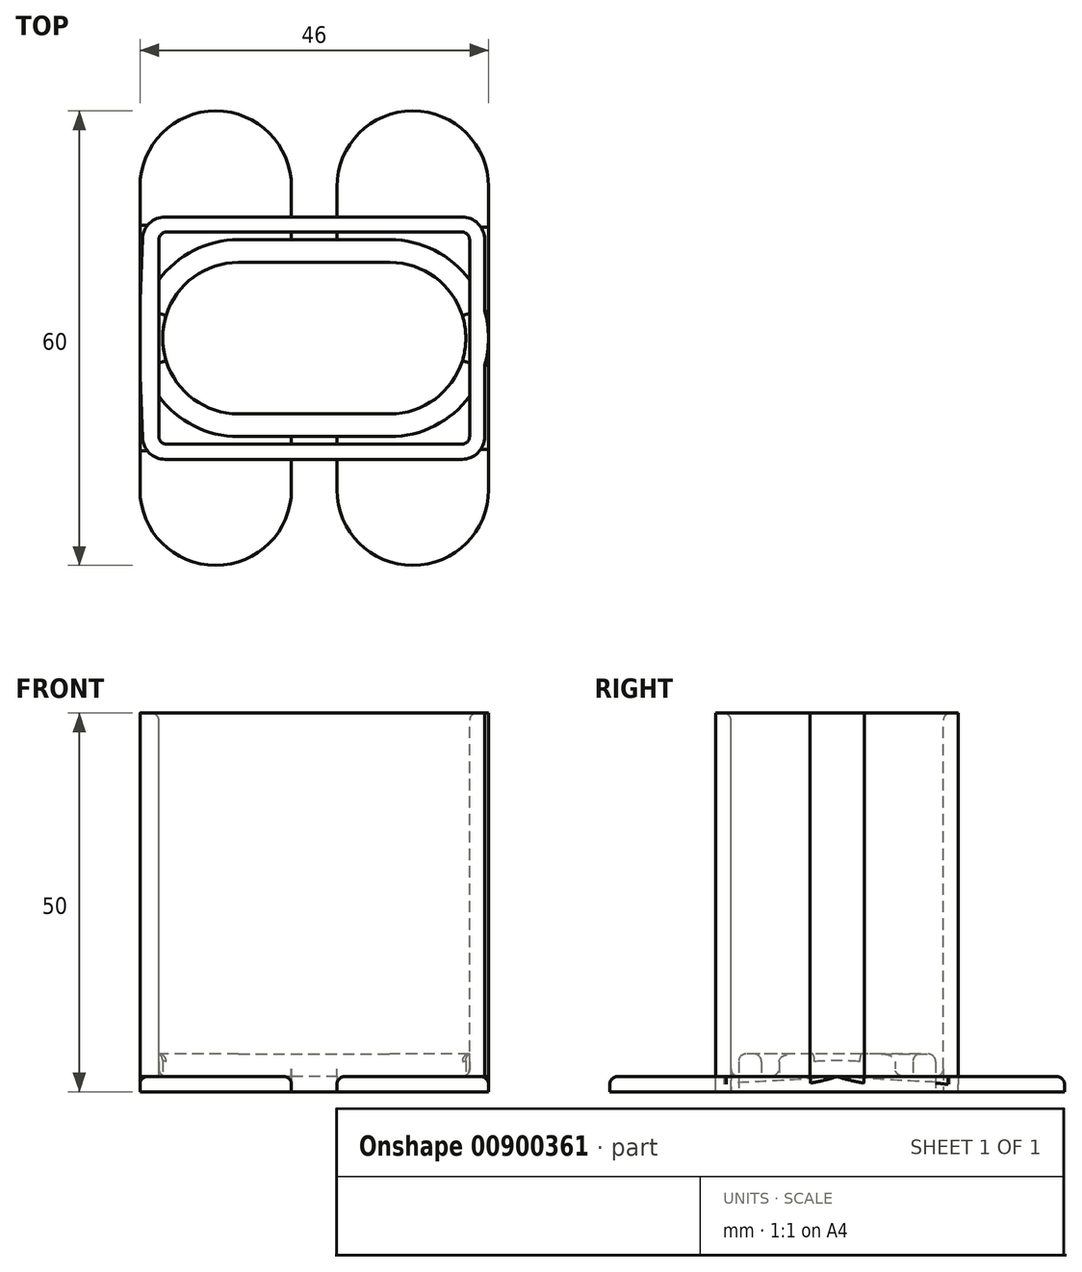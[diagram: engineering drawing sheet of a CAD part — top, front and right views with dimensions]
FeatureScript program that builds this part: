
annotation { "Feature Type Name" : "Feature", "Feature Type Description" : "" }
export const myFeature = defineFeature(function(context is Context, id is Id, definition is map)
    precondition{}
    {
        {
            var Q0;
            Q0=qCreatedBy(makeId("Top.planeOp"),FACE);
            var sketch = newSketch(context, id + "F0", { "sketchPlane" : qUnion([Q0])});
            skArc(sketch, "E0", {"start": v(-10, 10) * mm, "mid": v(-20, 0) * mm, "end": v(-10, -10) * mm});
            skLineSegment(sketch, "E1", {"start": v(-10, 10) * mm, "end": v(0, 10) * mm});
            skLineSegment(sketch, "E2", {"start": v(-10, -10) * mm, "end": v(0, -10) * mm});
            skArc(sketch, "E3", {"start": v(-10, 13) * mm, "mid": v(-23, 0) * mm, "end": v(-10, -13) * mm});
            skLineSegment(sketch, "E4", {"start": v(-10, 13) * mm, "end": v(0, 13) * mm});
            skLineSegment(sketch, "E5", {"start": v(-10, -13) * mm, "end": v(0, -13) * mm});
            skLineSegment(sketch, "E6", {"start": v(-23, 0) * mm, "end": v(-23, 20) * mm});
            skLineSegment(sketch, "E7", {"start": v(-23, 0) * mm, "end": v(-23, -20) * mm});
            skArc(sketch, "E8", {"start": v(-23, -20) * mm, "mid": v(-13, -30) * mm, "end": v(-3, -20) * mm});
            skArc(sketch, "E9", {"start": v(-3, 20) * mm, "mid": v(-13, 30) * mm, "end": v(-23, 20) * mm});
            skLineSegment(sketch, "E10", {"start": v(-3, 20) * mm, "end": v(-3, 13) * mm});
            skLineSegment(sketch, "E11", {"start": v(-3, -20) * mm, "end": v(-3, -13) * mm});
            skLineSegment(sketch, "E12.MirrorCS", {"start": v(3, -20) * mm, "end": v(3, -13) * mm});
            skLineSegment(sketch, "E13.MirrorCS", {"start": v(23, 0) * mm, "end": v(23, -20) * mm});
            skLineSegment(sketch, "E14.MirrorCS", {"start": v(10, -13) * mm, "end": v(0, -13) * mm});
            skArc(sketch, "E15.MirrorCS", {"start": v(23, -20) * mm, "mid": v(13, -30) * mm, "end": v(3, -20) * mm});
            skLineSegment(sketch, "E16.MirrorCS", {"start": v(3, 20) * mm, "end": v(3, 13) * mm});
            skLineSegment(sketch, "E17.MirrorCS", {"start": v(10, 10) * mm, "end": v(0, 10) * mm});
            skLineSegment(sketch, "E18.MirrorCS", {"start": v(10, 13) * mm, "end": v(0, 13) * mm});
            skArc(sketch, "E19.MirrorCS", {"start": v(10, 13) * mm, "mid": v(23, 0) * mm, "end": v(10, -13) * mm});
            skArc(sketch, "E20.MirrorCS", {"start": v(3, 20) * mm, "mid": v(13, 30) * mm, "end": v(23, 20) * mm});
            skArc(sketch, "E21.MirrorCS", {"start": v(10, 10) * mm, "mid": v(20, 0) * mm, "end": v(10, -10) * mm});
            skLineSegment(sketch, "E22.MirrorCS", {"start": v(23, 0) * mm, "end": v(23, 20) * mm});
            skLineSegment(sketch, "E23.MirrorCS", {"start": v(10, -10) * mm, "end": v(0, -10) * mm});
            skSolve(sketch);
        }
        {
            var Q0;
            Q0=makeQuery(id+"F0.imprint","IMPRINT",FACE,{"disambiguationData":[TD([[makeQuery(id+"F0.imprint","IMPRINT",EDGE,{"derivedFrom":sQuery(id+"F0.wireOp",EDGE,"E0")}),1.0]])]});
            var Q1;
            Q1=makeQuery(id+"F0.imprint","IMPRINT",FACE,{"disambiguationData":[TD([[makeQuery(id+"F0.imprint","IMPRINT",EDGE,{"derivedFrom":sQuery(id+"F0.wireOp",EDGE,"E0")}),-1.0]])]});
            var Q2;
            {var subQ0=sQuery(id+"F0.wireOp",EDGE,"E6");Q2=makeQuery(id+"F0.imprint","IMPRINT",FACE,{"disambiguationData":[TD([[makeQuery(id+"F0.imprint","IMPRINT",EDGE,{"derivedFrom":subQ0}),-1.0]])]});}
            var Q3;
            {var subQ0=sQuery(id+"F0.wireOp",EDGE,"E7");Q3=makeQuery(id+"F0.imprint","IMPRINT",FACE,{"disambiguationData":[TD([[makeQuery(id+"F0.imprint","IMPRINT",EDGE,{"derivedFrom":subQ0}),1.0]])]});}
            var Q4;
            {var subQ1=sQuery(id+"F0.wireOp",EDGE,"E12.MirrorCS");Q4=makeQuery(id+"F0.imprint","IMPRINT",FACE,{"disambiguationData":[TD([[makeQuery(id+"F0.imprint","IMPRINT",EDGE,{"derivedFrom":subQ1}),-1.0]])]});}
            var Q5;
            {var subQ4=sQuery(id+"F0.wireOp",EDGE,"E16.MirrorCS");Q5=makeQuery(id+"F0.imprint","IMPRINT",FACE,{"disambiguationData":[TD([[makeQuery(id+"F0.imprint","IMPRINT",EDGE,{"derivedFrom":subQ4}),1.0]])]});}
            extrude(context, id + "F1", {"entities" : qUnion([Q0, Q1, Q2, Q3, Q4, Q5]), "depth" : 2 * mm, "offsetDistance" : 25 * mm});
        }
        {
            var Q0;
            Q0=makeQuery(id+"F0.imprint","IMPRINT",FACE,{"disambiguationData":[TD([[makeQuery(id+"F0.imprint","IMPRINT",EDGE,{"derivedFrom":sQuery(id+"F0.wireOp",EDGE,"E0")}),-1.0]])]});
            extrude(context, id + "F2", {"entities" : qUnion([Q0]), "operationType" : NewBodyOperationType.ADD, "depth" : (2 + 3) * mm, "offsetDistance" : 25 * mm});
        }
        {
            var Q0;
            Q0=makeQuery(id+"F2.opExtrude","CAP_FACE",FACE,{"disambiguationData":[OSD([sQuery(id+"F0.wireOp",EDGE,"E0"),sQuery(id+"F0.wireOp",EDGE,"E1"),sQuery(id+"F0.wireOp",EDGE,"E2"),sQuery(id+"F0.wireOp",EDGE,"E3"),sQuery(id+"F0.wireOp",EDGE,"E4"),sQuery(id+"F0.wireOp",EDGE,"E5"),sQuery(id+"F0.wireOp",EDGE,"E14.MirrorCS"),sQuery(id+"F0.wireOp",EDGE,"E17.MirrorCS"),sQuery(id+"F0.wireOp",EDGE,"E18.MirrorCS"),sQuery(id+"F0.wireOp",EDGE,"E19.MirrorCS"),sQuery(id+"F0.wireOp",EDGE,"E21.MirrorCS"),sQuery(id+"F0.wireOp",EDGE,"E23.MirrorCS")])],"isStart":false});
            var sketch = newSketch(context, id + "F3", { "sketchPlane" : qUnion([Q0])});
            skLineSegment(sketch, "E24.bottom", {"start": v(-20.5, 14) * mm, "end": v(20.5, 14) * mm});
            skLineSegment(sketch, "E24.top", {"start": v(-20.5, -14) * mm, "end": v(20.5, -14) * mm});
            skLineSegment(sketch, "E24.left", {"start": v(-20.5, 14) * mm, "end": v(-20.5, -14) * mm});
            skLineSegment(sketch, "E24.right", {"start": v(20.5, 14) * mm, "end": v(20.5, -14) * mm});
            skPoint(sketch, "E25", {"position": v(0, 14) * mm});
            skPoint(sketch, "E26", {"position": v(20.5, 0) * mm});
            skLineSegment(sketch, "E27.bottom", {"start": v(-22.5, 16) * mm, "end": v(22.5, 16) * mm});
            skLineSegment(sketch, "E27.top", {"start": v(-22.5, -16) * mm, "end": v(22.5, -16) * mm});
            skLineSegment(sketch, "E27.left", {"start": v(-22.5, 16) * mm, "end": v(-22.5, -16) * mm});
            skLineSegment(sketch, "E27.right", {"start": v(22.5, 16) * mm, "end": v(22.5, -16) * mm});
            skPoint(sketch, "E27.middle", {"position": v(0, 0) * mm});
            skArc(sketch, "E28", {"start": v(-22.5, 16) * mm, "mid": v(-23, 0) * mm, "end": v(-22.5, -16) * mm});
            skArc(sketch, "E29", {"start": v(22.5, -16) * mm, "mid": v(23, 0) * mm, "end": v(22.5, 16) * mm});
            skSolve(sketch);
        }
        {
            var Q0;
            {var subQ0=sQuery(id+"F3.wireOp",EDGE,"E28");var subQ3=makeQuery(id+"F2.opExtrude","CAP_EDGE",EDGE,{"disambiguationData":[OSD([sQuery(id+"F0.wireOp",EDGE,"E3")])],"isStart":false});var subQ5=makeQuery(id+"F3.imprint","INTERSECT",VERTEX,{"derivedFrom":[subQ3,subQ0]});Q0=makeQuery(id+"F3.imprint","IMPRINT",FACE,{"disambiguationData":[TD([[makeQuery(id+"F3.imprint","IMPRINT",EDGE,{"disambiguationData":[TD([[subQ5,1.0]])],"derivedFrom":subQ3}),-1.0]])]});}
            var Q1;
            {var subQ0=sQuery(id+"F3.wireOp",EDGE,"E27.left");var subQ1=makeQuery(id+"F2.opExtrude","CAP_EDGE",EDGE,{"disambiguationData":[OSD([sQuery(id+"F0.wireOp",EDGE,"E3")])],"isStart":false});var subQ2=makeQuery(id+"F3.imprint","INTERSECT",VERTEX,{"disambiguationData":[OD(0.0)],"derivedFrom":[subQ1,subQ0]});Q1=makeQuery(id+"F3.imprint","IMPRINT",FACE,{"disambiguationData":[TD([[makeQuery(id+"F3.imprint","IMPRINT",EDGE,{"disambiguationData":[TD([[subQ2,-1.0]])],"derivedFrom":subQ0}),-1.0]])]});}
            var Q2;
            {var subQ0=sQuery(id+"F3.wireOp",EDGE,"E28");var subQ3=makeQuery(id+"F2.opExtrude","CAP_EDGE",EDGE,{"disambiguationData":[OSD([sQuery(id+"F0.wireOp",EDGE,"E3")])],"isStart":false});var subQ5=makeQuery(id+"F3.imprint","INTERSECT",VERTEX,{"derivedFrom":[subQ3,subQ0]});Q2=makeQuery(id+"F3.imprint","IMPRINT",FACE,{"disambiguationData":[TD([[makeQuery(id+"F3.imprint","IMPRINT",EDGE,{"disambiguationData":[TD([[subQ5,-1.0]])],"derivedFrom":subQ3}),-1.0]])]});}
            var Q3;
            {var subQ1=sQuery(id+"F3.wireOp",EDGE,"E24.top");Q3=makeQuery(id+"F3.imprint","IMPRINT",FACE,{"disambiguationData":[TD([[makeQuery(id+"F3.imprint","IMPRINT",EDGE,{"derivedFrom":subQ1}),-1.0]])]});}
            var Q4;
            {var subQ1=sQuery(id+"F3.wireOp",EDGE,"E24.bottom");Q4=makeQuery(id+"F3.imprint","IMPRINT",FACE,{"disambiguationData":[TD([[makeQuery(id+"F3.imprint","IMPRINT",EDGE,{"derivedFrom":subQ1}),1.0]])]});}
            var Q5;
            {var subQ0=sQuery(id+"F3.wireOp",EDGE,"E24.right");var subQ1=makeQuery(id+"F2.opExtrude","CAP_EDGE",EDGE,{"disambiguationData":[OSD([sQuery(id+"F0.wireOp",EDGE,"E19.MirrorCS")])],"isStart":false});var subQ2=makeQuery(id+"F3.imprint","INTERSECT",VERTEX,{"disambiguationData":[OD(0.0)],"derivedFrom":[subQ1,subQ0]});Q5=makeQuery(id+"F3.imprint","IMPRINT",FACE,{"disambiguationData":[TD([[makeQuery(id+"F3.imprint","IMPRINT",EDGE,{"disambiguationData":[TD([[subQ2,-1.0]])],"derivedFrom":subQ0}),1.0]])]});}
            var Q6;
            {var subQ0=sQuery(id+"F3.wireOp",EDGE,"E29");var subQ3=makeQuery(id+"F2.opExtrude","CAP_EDGE",EDGE,{"disambiguationData":[OSD([sQuery(id+"F0.wireOp",EDGE,"E19.MirrorCS")])],"isStart":false});var subQ5=makeQuery(id+"F3.imprint","INTERSECT",VERTEX,{"derivedFrom":[subQ3,subQ0]});Q6=makeQuery(id+"F3.imprint","IMPRINT",FACE,{"disambiguationData":[TD([[makeQuery(id+"F3.imprint","IMPRINT",EDGE,{"disambiguationData":[TD([[subQ5,1.0]])],"derivedFrom":subQ3}),1.0]])]});}
            var Q7;
            {var subQ0=sQuery(id+"F3.wireOp",EDGE,"E27.right");var subQ1=makeQuery(id+"F2.opExtrude","CAP_EDGE",EDGE,{"disambiguationData":[OSD([sQuery(id+"F0.wireOp",EDGE,"E19.MirrorCS")])],"isStart":false});var subQ2=makeQuery(id+"F3.imprint","INTERSECT",VERTEX,{"disambiguationData":[OD(0.0)],"derivedFrom":[subQ1,subQ0]});Q7=makeQuery(id+"F3.imprint","IMPRINT",FACE,{"disambiguationData":[TD([[makeQuery(id+"F3.imprint","IMPRINT",EDGE,{"disambiguationData":[TD([[subQ2,-1.0]])],"derivedFrom":subQ0}),1.0]])]});}
            var Q8;
            {var subQ0=sQuery(id+"F3.wireOp",EDGE,"E29");var subQ3=makeQuery(id+"F2.opExtrude","CAP_EDGE",EDGE,{"disambiguationData":[OSD([sQuery(id+"F0.wireOp",EDGE,"E19.MirrorCS")])],"isStart":false});var subQ5=makeQuery(id+"F3.imprint","INTERSECT",VERTEX,{"derivedFrom":[subQ3,subQ0]});Q8=makeQuery(id+"F3.imprint","IMPRINT",FACE,{"disambiguationData":[TD([[makeQuery(id+"F3.imprint","IMPRINT",EDGE,{"disambiguationData":[TD([[subQ5,-1.0]])],"derivedFrom":subQ3}),1.0]])]});}
            var Q9;
            {var subQ0=sQuery(id+"F3.wireOp",EDGE,"E24.left");var subQ1=makeQuery(id+"F2.opExtrude","CAP_EDGE",EDGE,{"disambiguationData":[OSD([sQuery(id+"F0.wireOp",EDGE,"E3")])],"isStart":false});var subQ2=makeQuery(id+"F3.imprint","INTERSECT",VERTEX,{"disambiguationData":[OD(0.0)],"derivedFrom":[subQ1,subQ0]});Q9=makeQuery(id+"F3.imprint","IMPRINT",FACE,{"disambiguationData":[TD([[makeQuery(id+"F3.imprint","IMPRINT",EDGE,{"disambiguationData":[TD([[subQ2,-1.0]])],"derivedFrom":subQ0}),-1.0]])]});}
            var Q10;
            {var subQ0=sQuery(id+"F0.wireOp",EDGE,"E8");var subQ1=sQuery(id+"F0.wireOp",EDGE,"E7");var subQ2=sQuery(id+"F0.wireOp",EDGE,"E6");var subQ3=sQuery(id+"F0.wireOp",EDGE,"E14.MirrorCS");var subQ4=sQuery(id+"F0.wireOp",EDGE,"E5");var subQ5=sQuery(id+"F0.wireOp",EDGE,"E11");var subQ6=makeQuery(id+"F1.opExtrude","CAP_FACE",FACE,{"disambiguationData":[OSD([sQuery(id+"F0.wireOp",EDGE,"E4"),subQ4,subQ2,subQ1,subQ0,sQuery(id+"F0.wireOp",EDGE,"E9"),sQuery(id+"F0.wireOp",EDGE,"E10"),subQ5,sQuery(id+"F0.wireOp",EDGE,"E12.MirrorCS"),sQuery(id+"F0.wireOp",EDGE,"E13.MirrorCS"),subQ3,sQuery(id+"F0.wireOp",EDGE,"E15.MirrorCS"),sQuery(id+"F0.wireOp",EDGE,"E16.MirrorCS"),sQuery(id+"F0.wireOp",EDGE,"E18.MirrorCS"),sQuery(id+"F0.wireOp",EDGE,"E20.MirrorCS"),sQuery(id+"F0.wireOp",EDGE,"E22.MirrorCS")])],"isStart":false});Q10=makeQuery(id+"F2.boolean.opBoolean","SPLIT",FACE,{"disambiguationData":[TD([makeQuery(id+"F1.opExtrude","SWEPT_FACE",FACE,{"disambiguationData":[OSD([subQ0])]})])],"derivedFrom":subQ6});}
            extrude(context, id + "F4", {"entities" : qUnion([Q0, Q1, Q2, Q3, Q4, Q5, Q6, Q7, Q8, Q9]), "operationType" : NewBodyOperationType.ADD, "endBound" : BoundingType.UP_TO_SURFACE, "oppositeDirection" : true, "depth" : 25 * mm, "endBoundEntityFace" : qUnion([Q10]), "offsetDistance" : 25 * mm});
        }
        {
            var Q0;
            {var subQ0=sQuery(id+"F3.wireOp",EDGE,"E28");var subQ3=makeQuery(id+"F2.opExtrude","CAP_EDGE",EDGE,{"disambiguationData":[OSD([sQuery(id+"F0.wireOp",EDGE,"E3")])],"isStart":false});var subQ5=makeQuery(id+"F3.imprint","INTERSECT",VERTEX,{"derivedFrom":[subQ3,subQ0]});Q0=makeQuery(id+"F3.imprint","IMPRINT",FACE,{"disambiguationData":[TD([[makeQuery(id+"F3.imprint","IMPRINT",EDGE,{"disambiguationData":[TD([[subQ5,1.0]])],"derivedFrom":subQ3}),-1.0]])]});}
            var Q1;
            {var subQ0=sQuery(id+"F3.wireOp",EDGE,"E27.left");var subQ1=makeQuery(id+"F2.opExtrude","CAP_EDGE",EDGE,{"disambiguationData":[OSD([sQuery(id+"F0.wireOp",EDGE,"E3")])],"isStart":false});var subQ2=makeQuery(id+"F3.imprint","INTERSECT",VERTEX,{"disambiguationData":[OD(0.0)],"derivedFrom":[subQ1,subQ0]});Q1=makeQuery(id+"F3.imprint","IMPRINT",FACE,{"disambiguationData":[TD([[makeQuery(id+"F3.imprint","IMPRINT",EDGE,{"disambiguationData":[TD([[subQ2,-1.0]])],"derivedFrom":subQ0}),-1.0]])]});}
            var Q2;
            {var subQ0=sQuery(id+"F3.wireOp",EDGE,"E28");var subQ3=makeQuery(id+"F2.opExtrude","CAP_EDGE",EDGE,{"disambiguationData":[OSD([sQuery(id+"F0.wireOp",EDGE,"E3")])],"isStart":false});var subQ5=makeQuery(id+"F3.imprint","INTERSECT",VERTEX,{"derivedFrom":[subQ3,subQ0]});Q2=makeQuery(id+"F3.imprint","IMPRINT",FACE,{"disambiguationData":[TD([[makeQuery(id+"F3.imprint","IMPRINT",EDGE,{"disambiguationData":[TD([[subQ5,-1.0]])],"derivedFrom":subQ3}),-1.0]])]});}
            var Q3;
            {var subQ1=sQuery(id+"F3.wireOp",EDGE,"E24.bottom");Q3=makeQuery(id+"F3.imprint","IMPRINT",FACE,{"disambiguationData":[TD([[makeQuery(id+"F3.imprint","IMPRINT",EDGE,{"derivedFrom":subQ1}),1.0]])]});}
            var Q4;
            {var subQ0=sQuery(id+"F3.wireOp",EDGE,"E24.left");var subQ1=makeQuery(id+"F2.opExtrude","CAP_EDGE",EDGE,{"disambiguationData":[OSD([sQuery(id+"F0.wireOp",EDGE,"E3")])],"isStart":false});var subQ2=makeQuery(id+"F3.imprint","INTERSECT",VERTEX,{"disambiguationData":[OD(0.0)],"derivedFrom":[subQ1,subQ0]});Q4=makeQuery(id+"F3.imprint","IMPRINT",FACE,{"disambiguationData":[TD([[makeQuery(id+"F3.imprint","IMPRINT",EDGE,{"disambiguationData":[TD([[subQ2,-1.0]])],"derivedFrom":subQ0}),-1.0]])]});}
            var Q5;
            {var subQ1=sQuery(id+"F3.wireOp",EDGE,"E24.top");Q5=makeQuery(id+"F3.imprint","IMPRINT",FACE,{"disambiguationData":[TD([[makeQuery(id+"F3.imprint","IMPRINT",EDGE,{"derivedFrom":subQ1}),-1.0]])]});}
            var Q6;
            {var subQ0=sQuery(id+"F3.wireOp",EDGE,"E29");var subQ3=makeQuery(id+"F2.opExtrude","CAP_EDGE",EDGE,{"disambiguationData":[OSD([sQuery(id+"F0.wireOp",EDGE,"E19.MirrorCS")])],"isStart":false});var subQ5=makeQuery(id+"F3.imprint","INTERSECT",VERTEX,{"derivedFrom":[subQ3,subQ0]});Q6=makeQuery(id+"F3.imprint","IMPRINT",FACE,{"disambiguationData":[TD([[makeQuery(id+"F3.imprint","IMPRINT",EDGE,{"disambiguationData":[TD([[subQ5,1.0]])],"derivedFrom":subQ3}),1.0]])]});}
            var Q7;
            {var subQ0=sQuery(id+"F3.wireOp",EDGE,"E27.right");var subQ1=makeQuery(id+"F2.opExtrude","CAP_EDGE",EDGE,{"disambiguationData":[OSD([sQuery(id+"F0.wireOp",EDGE,"E19.MirrorCS")])],"isStart":false});var subQ2=makeQuery(id+"F3.imprint","INTERSECT",VERTEX,{"disambiguationData":[OD(0.0)],"derivedFrom":[subQ1,subQ0]});Q7=makeQuery(id+"F3.imprint","IMPRINT",FACE,{"disambiguationData":[TD([[makeQuery(id+"F3.imprint","IMPRINT",EDGE,{"disambiguationData":[TD([[subQ2,-1.0]])],"derivedFrom":subQ0}),1.0]])]});}
            var Q8;
            {var subQ0=sQuery(id+"F3.wireOp",EDGE,"E29");var subQ3=makeQuery(id+"F2.opExtrude","CAP_EDGE",EDGE,{"disambiguationData":[OSD([sQuery(id+"F0.wireOp",EDGE,"E19.MirrorCS")])],"isStart":false});var subQ5=makeQuery(id+"F3.imprint","INTERSECT",VERTEX,{"derivedFrom":[subQ3,subQ0]});Q8=makeQuery(id+"F3.imprint","IMPRINT",FACE,{"disambiguationData":[TD([[makeQuery(id+"F3.imprint","IMPRINT",EDGE,{"disambiguationData":[TD([[subQ5,-1.0]])],"derivedFrom":subQ3}),1.0]])]});}
            var Q9;
            {var subQ0=sQuery(id+"F3.wireOp",EDGE,"E24.right");var subQ1=makeQuery(id+"F2.opExtrude","CAP_EDGE",EDGE,{"disambiguationData":[OSD([sQuery(id+"F0.wireOp",EDGE,"E19.MirrorCS")])],"isStart":false});var subQ2=makeQuery(id+"F3.imprint","INTERSECT",VERTEX,{"disambiguationData":[OD(0.0)],"derivedFrom":[subQ1,subQ0]});Q9=makeQuery(id+"F3.imprint","IMPRINT",FACE,{"disambiguationData":[TD([[makeQuery(id+"F3.imprint","IMPRINT",EDGE,{"disambiguationData":[TD([[subQ2,-1.0]])],"derivedFrom":subQ0}),1.0]])]});}
            extrude(context, id + "F5", {"entities" : qUnion([Q0, Q1, Q2, Q3, Q4, Q5, Q6, Q7, Q8, Q9]), "operationType" : NewBodyOperationType.ADD, "depth" : (25 + 20) * mm, "offsetDistance" : 25 * mm});
        }
        {
            var Q0;
            {var subQ0=sQuery(id+"F3.wireOp",EDGE,"E28");var subQ1=sQuery(id+"F3.wireOp",EDGE,"E27.left");var subQ2=sQuery(id+"F3.wireOp",EDGE,"E27.bottom");Q0=makeQuery(id+"F5.boolean.opBoolean","MERGE",EDGE,{"derivedFrom":[makeQuery(id+"F4.opExtrude","SWEPT_EDGE",EDGE,{"disambiguationData":[OSD([subQ2,subQ1,subQ0])]}),makeQuery(id+"F5.opExtrude","SWEPT_EDGE",EDGE,{"disambiguationData":[OSD([subQ2,subQ1,subQ0])]})]});}
            var Q1;
            {var subQ0=sQuery(id+"F3.wireOp",EDGE,"E28");var subQ1=sQuery(id+"F3.wireOp",EDGE,"E27.left");var subQ2=sQuery(id+"F3.wireOp",EDGE,"E27.top");Q1=makeQuery(id+"F5.boolean.opBoolean","MERGE",EDGE,{"derivedFrom":[makeQuery(id+"F4.opExtrude","SWEPT_EDGE",EDGE,{"disambiguationData":[OSD([subQ2,subQ1,subQ0])]}),makeQuery(id+"F5.opExtrude","SWEPT_EDGE",EDGE,{"disambiguationData":[OSD([subQ2,subQ1,subQ0])]})]});}
            var Q2;
            {var subQ0=sQuery(id+"F3.wireOp",EDGE,"E29");var subQ1=sQuery(id+"F3.wireOp",EDGE,"E27.right");var subQ2=sQuery(id+"F3.wireOp",EDGE,"E27.bottom");Q2=makeQuery(id+"F5.boolean.opBoolean","MERGE",EDGE,{"derivedFrom":[makeQuery(id+"F4.opExtrude","SWEPT_EDGE",EDGE,{"disambiguationData":[OSD([subQ2,subQ1,subQ0])]}),makeQuery(id+"F5.opExtrude","SWEPT_EDGE",EDGE,{"disambiguationData":[OSD([subQ2,subQ1,subQ0])]})]});}
            var Q3;
            {var subQ0=sQuery(id+"F3.wireOp",EDGE,"E29");var subQ1=sQuery(id+"F3.wireOp",EDGE,"E27.right");var subQ2=sQuery(id+"F3.wireOp",EDGE,"E27.top");Q3=makeQuery(id+"F5.boolean.opBoolean","MERGE",EDGE,{"derivedFrom":[makeQuery(id+"F4.opExtrude","SWEPT_EDGE",EDGE,{"disambiguationData":[OSD([subQ2,subQ1,subQ0])]}),makeQuery(id+"F5.opExtrude","SWEPT_EDGE",EDGE,{"disambiguationData":[OSD([subQ2,subQ1,subQ0])]})]});}
            fillet(context, id + "F6", {"entities" : qUnion([Q0, Q1, Q2, Q3]), "radius" : 3 * mm, "tangentPropagation" : true, "allowEdgeOverflow" : false});
        }
        {
            var Q0;
            {var subQ0=sQuery(id+"F3.wireOp",EDGE,"E24.right");var subQ1=sQuery(id+"F3.wireOp",EDGE,"E24.top");Q0=makeQuery(id+"F5.boolean.opBoolean","MERGE",EDGE,{"derivedFrom":[makeQuery(id+"F4.opExtrude","SWEPT_EDGE",EDGE,{"disambiguationData":[OSD([subQ1,subQ0])]}),makeQuery(id+"F5.opExtrude","SWEPT_EDGE",EDGE,{"disambiguationData":[OSD([subQ1,subQ0])]})]});}
            var Q1;
            {var subQ0=sQuery(id+"F3.wireOp",EDGE,"E24.left");var subQ1=sQuery(id+"F3.wireOp",EDGE,"E24.top");Q1=makeQuery(id+"F5.boolean.opBoolean","MERGE",EDGE,{"derivedFrom":[makeQuery(id+"F4.opExtrude","SWEPT_EDGE",EDGE,{"disambiguationData":[OSD([subQ1,subQ0])]}),makeQuery(id+"F5.opExtrude","SWEPT_EDGE",EDGE,{"disambiguationData":[OSD([subQ1,subQ0])]})]});}
            var Q2;
            {var subQ0=sQuery(id+"F3.wireOp",EDGE,"E24.left");var subQ1=sQuery(id+"F3.wireOp",EDGE,"E24.bottom");Q2=makeQuery(id+"F5.boolean.opBoolean","MERGE",EDGE,{"derivedFrom":[makeQuery(id+"F4.opExtrude","SWEPT_EDGE",EDGE,{"disambiguationData":[OSD([subQ1,subQ0])]}),makeQuery(id+"F5.opExtrude","SWEPT_EDGE",EDGE,{"disambiguationData":[OSD([subQ1,subQ0])]})]});}
            var Q3;
            {var subQ0=sQuery(id+"F3.wireOp",EDGE,"E24.right");var subQ1=sQuery(id+"F3.wireOp",EDGE,"E24.bottom");Q3=makeQuery(id+"F5.boolean.opBoolean","MERGE",EDGE,{"derivedFrom":[makeQuery(id+"F4.opExtrude","SWEPT_EDGE",EDGE,{"disambiguationData":[OSD([subQ1,subQ0])]}),makeQuery(id+"F5.opExtrude","SWEPT_EDGE",EDGE,{"disambiguationData":[OSD([subQ1,subQ0])]})]});}
            var Q4;
            {var subQ0=sQuery(id+"F3.wireOp",EDGE,"E24.right");Q4=makeQuery(id+"F4.boolean.opBoolean","SPLIT",EDGE,{"disambiguationData":[TD([makeQuery(id+"F4.opExtrude","SWEPT_FACE",FACE,{"disambiguationData":[OSD([sQuery(id+"F3.wireOp",EDGE,"E24.bottom")])]})])],"derivedFrom":makeQuery(id+"F4.opExtrude","CAP_EDGE",EDGE,{"disambiguationData":[OSD([subQ0])],"isStart":false})});}
            var Q5;
            {var subQ0=sQuery(id+"F3.wireOp",EDGE,"E24.bottom");var subQ1=makeQuery(id+"F4.opExtrude","SWEPT_FACE",FACE,{"disambiguationData":[OSD([subQ0])]});var subQ3=sQuery(id+"F0.wireOp",EDGE,"E16.MirrorCS");var subQ4=makeQuery(id+"F1.opExtrude","CAP_FACE",FACE,{"disambiguationData":[OSD([sQuery(id+"F0.wireOp",EDGE,"E4"),sQuery(id+"F0.wireOp",EDGE,"E5"),sQuery(id+"F0.wireOp",EDGE,"E6"),sQuery(id+"F0.wireOp",EDGE,"E7"),sQuery(id+"F0.wireOp",EDGE,"E8"),sQuery(id+"F0.wireOp",EDGE,"E9"),sQuery(id+"F0.wireOp",EDGE,"E10"),sQuery(id+"F0.wireOp",EDGE,"E11"),sQuery(id+"F0.wireOp",EDGE,"E12.MirrorCS"),sQuery(id+"F0.wireOp",EDGE,"E13.MirrorCS"),sQuery(id+"F0.wireOp",EDGE,"E14.MirrorCS"),sQuery(id+"F0.wireOp",EDGE,"E15.MirrorCS"),subQ3,sQuery(id+"F0.wireOp",EDGE,"E18.MirrorCS"),sQuery(id+"F0.wireOp",EDGE,"E20.MirrorCS"),sQuery(id+"F0.wireOp",EDGE,"E22.MirrorCS")])],"isStart":false});Q5=makeQuery(id+"F4.boolean.opBoolean","SPLIT",EDGE,{"disambiguationData":[topologyDisambiguationEdgeConnected([subQ4,subQ1]),TD([makeQuery(id+"F1.opExtrude","SWEPT_FACE",FACE,{"disambiguationData":[OSD([subQ3])]})])],"derivedFrom":makeQuery(id+"F4.opExtrude","CAP_EDGE",EDGE,{"disambiguationData":[OSD([subQ0])],"isStart":false})});}
            var Q6;
            {var subQ0=sQuery(id+"F3.wireOp",EDGE,"E24.bottom");var subQ1=makeQuery(id+"F4.opExtrude","SWEPT_FACE",FACE,{"disambiguationData":[OSD([subQ0])]});var subQ3=sQuery(id+"F0.wireOp",EDGE,"E10");var subQ4=makeQuery(id+"F1.opExtrude","CAP_FACE",FACE,{"disambiguationData":[OSD([sQuery(id+"F0.wireOp",EDGE,"E4"),sQuery(id+"F0.wireOp",EDGE,"E5"),sQuery(id+"F0.wireOp",EDGE,"E6"),sQuery(id+"F0.wireOp",EDGE,"E7"),sQuery(id+"F0.wireOp",EDGE,"E8"),sQuery(id+"F0.wireOp",EDGE,"E9"),subQ3,sQuery(id+"F0.wireOp",EDGE,"E11"),sQuery(id+"F0.wireOp",EDGE,"E12.MirrorCS"),sQuery(id+"F0.wireOp",EDGE,"E13.MirrorCS"),sQuery(id+"F0.wireOp",EDGE,"E14.MirrorCS"),sQuery(id+"F0.wireOp",EDGE,"E15.MirrorCS"),sQuery(id+"F0.wireOp",EDGE,"E16.MirrorCS"),sQuery(id+"F0.wireOp",EDGE,"E18.MirrorCS"),sQuery(id+"F0.wireOp",EDGE,"E20.MirrorCS"),sQuery(id+"F0.wireOp",EDGE,"E22.MirrorCS")])],"isStart":false});Q6=makeQuery(id+"F4.boolean.opBoolean","SPLIT",EDGE,{"disambiguationData":[topologyDisambiguationEdgeConnected([subQ4,subQ1]),TD([makeQuery(id+"F1.opExtrude","SWEPT_FACE",FACE,{"disambiguationData":[OSD([subQ3])]})])],"derivedFrom":makeQuery(id+"F4.opExtrude","CAP_EDGE",EDGE,{"disambiguationData":[OSD([subQ0])],"isStart":false})});}
            var Q7;
            {var subQ0=sQuery(id+"F3.wireOp",EDGE,"E24.left");Q7=makeQuery(id+"F4.boolean.opBoolean","SPLIT",EDGE,{"disambiguationData":[TD([makeQuery(id+"F4.opExtrude","SWEPT_FACE",FACE,{"disambiguationData":[OSD([sQuery(id+"F3.wireOp",EDGE,"E24.bottom")])]})])],"derivedFrom":makeQuery(id+"F4.opExtrude","CAP_EDGE",EDGE,{"disambiguationData":[OSD([subQ0])],"isStart":false})});}
            var Q8;
            {var subQ0=sQuery(id+"F3.wireOp",EDGE,"E24.left");Q8=makeQuery(id+"F4.boolean.opBoolean","SPLIT",EDGE,{"disambiguationData":[TD([makeQuery(id+"F4.opExtrude","SWEPT_FACE",FACE,{"disambiguationData":[OSD([sQuery(id+"F3.wireOp",EDGE,"E24.top")])]})])],"derivedFrom":makeQuery(id+"F4.opExtrude","CAP_EDGE",EDGE,{"disambiguationData":[OSD([subQ0])],"isStart":false})});}
            var Q9;
            {var subQ1=sQuery(id+"F3.wireOp",EDGE,"E24.top");var subQ2=makeQuery(id+"F4.opExtrude","SWEPT_FACE",FACE,{"disambiguationData":[OSD([subQ1])]});var subQ3=sQuery(id+"F0.wireOp",EDGE,"E11");var subQ4=makeQuery(id+"F1.opExtrude","CAP_FACE",FACE,{"disambiguationData":[OSD([sQuery(id+"F0.wireOp",EDGE,"E4"),sQuery(id+"F0.wireOp",EDGE,"E5"),sQuery(id+"F0.wireOp",EDGE,"E6"),sQuery(id+"F0.wireOp",EDGE,"E7"),sQuery(id+"F0.wireOp",EDGE,"E8"),sQuery(id+"F0.wireOp",EDGE,"E9"),sQuery(id+"F0.wireOp",EDGE,"E10"),subQ3,sQuery(id+"F0.wireOp",EDGE,"E12.MirrorCS"),sQuery(id+"F0.wireOp",EDGE,"E13.MirrorCS"),sQuery(id+"F0.wireOp",EDGE,"E14.MirrorCS"),sQuery(id+"F0.wireOp",EDGE,"E15.MirrorCS"),sQuery(id+"F0.wireOp",EDGE,"E16.MirrorCS"),sQuery(id+"F0.wireOp",EDGE,"E18.MirrorCS"),sQuery(id+"F0.wireOp",EDGE,"E20.MirrorCS"),sQuery(id+"F0.wireOp",EDGE,"E22.MirrorCS")])],"isStart":false});Q9=makeQuery(id+"F4.boolean.opBoolean","SPLIT",EDGE,{"disambiguationData":[topologyDisambiguationEdgeConnected([subQ4,subQ2]),TD([makeQuery(id+"F1.opExtrude","SWEPT_FACE",FACE,{"disambiguationData":[OSD([subQ3])]})])],"derivedFrom":makeQuery(id+"F4.opExtrude","CAP_EDGE",EDGE,{"disambiguationData":[OSD([subQ1])],"isStart":false})});}
            var Q10;
            {var subQ0=sQuery(id+"F3.wireOp",EDGE,"E24.top");var subQ1=makeQuery(id+"F4.opExtrude","SWEPT_FACE",FACE,{"disambiguationData":[OSD([subQ0])]});var subQ2=sQuery(id+"F0.wireOp",EDGE,"E12.MirrorCS");var subQ3=makeQuery(id+"F1.opExtrude","CAP_FACE",FACE,{"disambiguationData":[OSD([sQuery(id+"F0.wireOp",EDGE,"E4"),sQuery(id+"F0.wireOp",EDGE,"E5"),sQuery(id+"F0.wireOp",EDGE,"E6"),sQuery(id+"F0.wireOp",EDGE,"E7"),sQuery(id+"F0.wireOp",EDGE,"E8"),sQuery(id+"F0.wireOp",EDGE,"E9"),sQuery(id+"F0.wireOp",EDGE,"E10"),sQuery(id+"F0.wireOp",EDGE,"E11"),subQ2,sQuery(id+"F0.wireOp",EDGE,"E13.MirrorCS"),sQuery(id+"F0.wireOp",EDGE,"E14.MirrorCS"),sQuery(id+"F0.wireOp",EDGE,"E15.MirrorCS"),sQuery(id+"F0.wireOp",EDGE,"E16.MirrorCS"),sQuery(id+"F0.wireOp",EDGE,"E18.MirrorCS"),sQuery(id+"F0.wireOp",EDGE,"E20.MirrorCS"),sQuery(id+"F0.wireOp",EDGE,"E22.MirrorCS")])],"isStart":false});Q10=makeQuery(id+"F4.boolean.opBoolean","SPLIT",EDGE,{"disambiguationData":[topologyDisambiguationEdgeConnected([subQ3,subQ1]),TD([makeQuery(id+"F1.opExtrude","SWEPT_FACE",FACE,{"disambiguationData":[OSD([subQ2])]})])],"derivedFrom":makeQuery(id+"F4.opExtrude","CAP_EDGE",EDGE,{"disambiguationData":[OSD([subQ0])],"isStart":false})});}
            var Q11;
            {var subQ0=sQuery(id+"F3.wireOp",EDGE,"E24.right");Q11=makeQuery(id+"F4.boolean.opBoolean","SPLIT",EDGE,{"disambiguationData":[TD([makeQuery(id+"F4.opExtrude","SWEPT_FACE",FACE,{"disambiguationData":[OSD([sQuery(id+"F3.wireOp",EDGE,"E24.top")])]})])],"derivedFrom":makeQuery(id+"F4.opExtrude","CAP_EDGE",EDGE,{"disambiguationData":[OSD([subQ0])],"isStart":false})});}
            var Q12;
            {var subQ0=sQuery(id+"F0.wireOp",EDGE,"E19.MirrorCS");var subQ1=sQuery(id+"F0.wireOp",EDGE,"E14.MirrorCS");var subQ2=sQuery(id+"F0.wireOp",EDGE,"E5");Q12=makeQuery(id+"F4.boolean.opBoolean","SPLIT",EDGE,{"disambiguationData":[TD([makeQuery(id+"F1.opExtrude","SWEPT_FACE",FACE,{"disambiguationData":[OSD([subQ2,subQ1])]})])],"derivedFrom":makeQuery(id+"F2.opExtrude","CAP_EDGE",EDGE,{"disambiguationData":[OSD([subQ0])],"isStart":false})});}
            var Q13;
            {var subQ0=sQuery(id+"F0.wireOp",EDGE,"E19.MirrorCS");var subQ1=sQuery(id+"F0.wireOp",EDGE,"E18.MirrorCS");var subQ2=sQuery(id+"F0.wireOp",EDGE,"E4");Q13=makeQuery(id+"F4.boolean.opBoolean","SPLIT",EDGE,{"disambiguationData":[TD([makeQuery(id+"F1.opExtrude","SWEPT_FACE",FACE,{"disambiguationData":[OSD([subQ2,subQ1])]})])],"derivedFrom":makeQuery(id+"F2.opExtrude","CAP_EDGE",EDGE,{"disambiguationData":[OSD([subQ0])],"isStart":false})});}
            var Q14;
            Q14=makeQuery(id+"F5.boolean.opBoolean","SPLIT",EDGE,{"disambiguationData":[OD(0.0)],"derivedFrom":makeQuery(id+"F5.opExtrude","CAP_EDGE",EDGE,{"disambiguationData":[OSD([sQuery(id+"F3.wireOp",EDGE,"E24.right")])],"isStart":true})});
            var Q15;
            Q15=makeQuery(id+"F5.boolean.opBoolean","SPLIT",EDGE,{"disambiguationData":[OD(1.0)],"derivedFrom":makeQuery(id+"F5.opExtrude","CAP_EDGE",EDGE,{"disambiguationData":[OSD([sQuery(id+"F3.wireOp",EDGE,"E24.left")])],"isStart":true})});
            fillet(context, id + "F7", {"entities" : qUnion([Q0, Q1, Q2, Q3, Q4, Q5, Q6, Q7, Q8, Q9, Q10, Q11, Q12, Q13, Q14, Q15]), "radius" : 1 * mm, "tangentPropagation" : true, "allowEdgeOverflow" : false});
        }
        {
            var Q0;
            Q0=makeQuery(id+"F7.opFillet","BLEND_EDGE",EDGE,{"blendedFrom":[makeQuery(id+"F5.boolean.opBoolean","SPLIT",EDGE,{"disambiguationData":[OD(1.0)],"derivedFrom":makeQuery(id+"F5.opExtrude","CAP_EDGE",EDGE,{"disambiguationData":[OSD([sQuery(id+"F3.wireOp",EDGE,"E24.left")])],"isStart":true})}),makeQuery(id+"F2.opExtrude","SWEPT_FACE",FACE,{"disambiguationData":[OSD([sQuery(id+"F0.wireOp",EDGE,"E0")])]})],"blendedInto":[makeQuery(id+"F2.opExtrude","SWEPT_FACE",FACE,{"disambiguationData":[OSD([sQuery(id+"F0.wireOp",EDGE,"E0")])]})]});
            var Q1;
            {var subQ1=sQuery(id+"F0.wireOp",EDGE,"E21.MirrorCS");var subQ2=sQuery(id+"F0.wireOp",EDGE,"E17.MirrorCS");var subQ3=sQuery(id+"F0.wireOp",EDGE,"E1");Q1=makeQuery(id+"F5.boolean.opBoolean","SPLIT",EDGE,{"disambiguationData":[TD([makeQuery(id+"F2.opExtrude","SWEPT_FACE",FACE,{"disambiguationData":[OSD([subQ3,subQ2])]})])],"derivedFrom":makeQuery(id+"F2.opExtrude","CAP_EDGE",EDGE,{"disambiguationData":[OSD([subQ1])],"isStart":false})});}
            var Q2;
            Q2=makeQuery(id+"F5.opExtrude","CAP_EDGE",EDGE,{"disambiguationData":[OSD([sQuery(id+"F3.wireOp",EDGE,"E29")])],"isStart":false});
            var Q3;
            Q3=makeQuery(id+"F5.opExtrude","CAP_EDGE",EDGE,{"disambiguationData":[OSD([sQuery(id+"F3.wireOp",EDGE,"E24.right")])],"isStart":false});
            var Q4;
            Q4=makeQuery(id+"F1.opExtrude","CAP_EDGE",EDGE,{"disambiguationData":[OSD([sQuery(id+"F0.wireOp",EDGE,"E15.MirrorCS")])],"isStart":false});
            var Q5;
            Q5=makeQuery(id+"F1.opExtrude","CAP_EDGE",EDGE,{"disambiguationData":[OSD([sQuery(id+"F0.wireOp",EDGE,"E8")])],"isStart":false});
            fillet(context, id + "F8", {"entities" : qUnion([Q0, Q1, Q2, Q3, Q4, Q5]), "radius" : 1 * mm, "tangentPropagation" : true, "allowEdgeOverflow" : false});
        }
        {
            var Q0;
            {var subQ0=sQuery(id+"F3.wireOp",EDGE,"E24.bottom");var subQ2=sQuery(id+"F0.wireOp",EDGE,"E10");var subQ3=sQuery(id+"F3.wireOp",EDGE,"E27.bottom");Q0=makeQuery(id+"F4.boolean.opBoolean","SPLIT",FACE,{"disambiguationData":[TD([makeQuery(id+"F1.opExtrude","SWEPT_FACE",FACE,{"disambiguationData":[OSD([subQ2])]})])],"derivedFrom":makeQuery(id+"F4.opExtrude","CAP_FACE",FACE,{"disambiguationData":[OSD([subQ0,sQuery(id+"F3.wireOp",EDGE,"E24.top"),sQuery(id+"F3.wireOp",EDGE,"E24.left"),sQuery(id+"F3.wireOp",EDGE,"E24.right"),subQ3,sQuery(id+"F3.wireOp",EDGE,"E27.top"),sQuery(id+"F3.wireOp",EDGE,"E28"),sQuery(id+"F3.wireOp",EDGE,"E29")])],"isStart":false})});}
            var Q1;
            {var subQ1=sQuery(id+"F3.wireOp",EDGE,"E24.top");var subQ2=sQuery(id+"F0.wireOp",EDGE,"E11");var subQ3=sQuery(id+"F3.wireOp",EDGE,"E27.top");Q1=makeQuery(id+"F4.boolean.opBoolean","SPLIT",FACE,{"disambiguationData":[TD([makeQuery(id+"F1.opExtrude","SWEPT_FACE",FACE,{"disambiguationData":[OSD([subQ2])]})])],"derivedFrom":makeQuery(id+"F4.opExtrude","CAP_FACE",FACE,{"disambiguationData":[OSD([sQuery(id+"F3.wireOp",EDGE,"E24.bottom"),subQ1,sQuery(id+"F3.wireOp",EDGE,"E24.left"),sQuery(id+"F3.wireOp",EDGE,"E24.right"),sQuery(id+"F3.wireOp",EDGE,"E27.bottom"),subQ3,sQuery(id+"F3.wireOp",EDGE,"E28"),sQuery(id+"F3.wireOp",EDGE,"E29")])],"isStart":false})});}
            var Q2;
            Q2=makeQuery(id+"F1.opExtrude","CAP_FACE",FACE,{"disambiguationData":[OSD([sQuery(id+"F0.wireOp",EDGE,"E4"),sQuery(id+"F0.wireOp",EDGE,"E5"),sQuery(id+"F0.wireOp",EDGE,"E6"),sQuery(id+"F0.wireOp",EDGE,"E7"),sQuery(id+"F0.wireOp",EDGE,"E8"),sQuery(id+"F0.wireOp",EDGE,"E9"),sQuery(id+"F0.wireOp",EDGE,"E10"),sQuery(id+"F0.wireOp",EDGE,"E11"),sQuery(id+"F0.wireOp",EDGE,"E12.MirrorCS"),sQuery(id+"F0.wireOp",EDGE,"E13.MirrorCS"),sQuery(id+"F0.wireOp",EDGE,"E14.MirrorCS"),sQuery(id+"F0.wireOp",EDGE,"E15.MirrorCS"),sQuery(id+"F0.wireOp",EDGE,"E16.MirrorCS"),sQuery(id+"F0.wireOp",EDGE,"E18.MirrorCS"),sQuery(id+"F0.wireOp",EDGE,"E20.MirrorCS"),sQuery(id+"F0.wireOp",EDGE,"E22.MirrorCS")])],"isStart":true});
            extrude(context, id + "F9", {"entities" : qUnion([Q0, Q1]), "operationType" : NewBodyOperationType.ADD, "endBound" : BoundingType.UP_TO_SURFACE, "depth" : 25 * mm, "endBoundEntityFace" : qUnion([Q2]), "offsetDistance" : 25 * mm});
        }
    });
